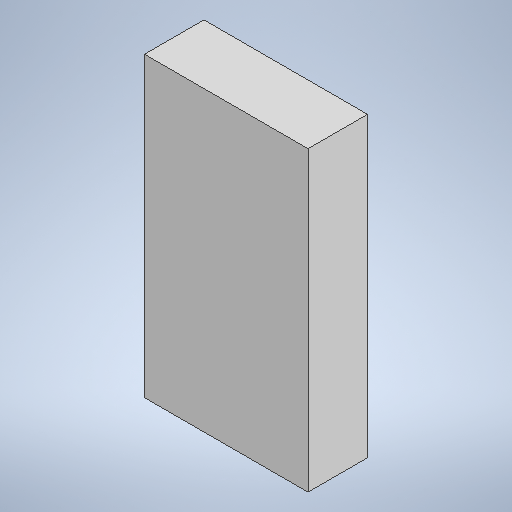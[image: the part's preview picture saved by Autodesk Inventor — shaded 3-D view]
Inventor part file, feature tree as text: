
AUTODESK INVENTOR PART (.ipt)
format: ipt  version: 2025 (Build 290162010, 162A)  size: 207,872 bytes
history: native  units: mm
features: extrude x1, sketch x1
ambient origin geometry x8: Origin, YZ Plane, XZ Plane, XY Plane, X Axis, Y Axis, Z Axis, Center Point
bodies: Solid1 (feature_tree)
feature tree (2):
  extrude  "Extrusion1"  Depth=400.0mm
  sketch  "Sketch1"  dims[d0=1100.0mm d1=400.0mm d2=2000.0mm d3=0.0mm]
